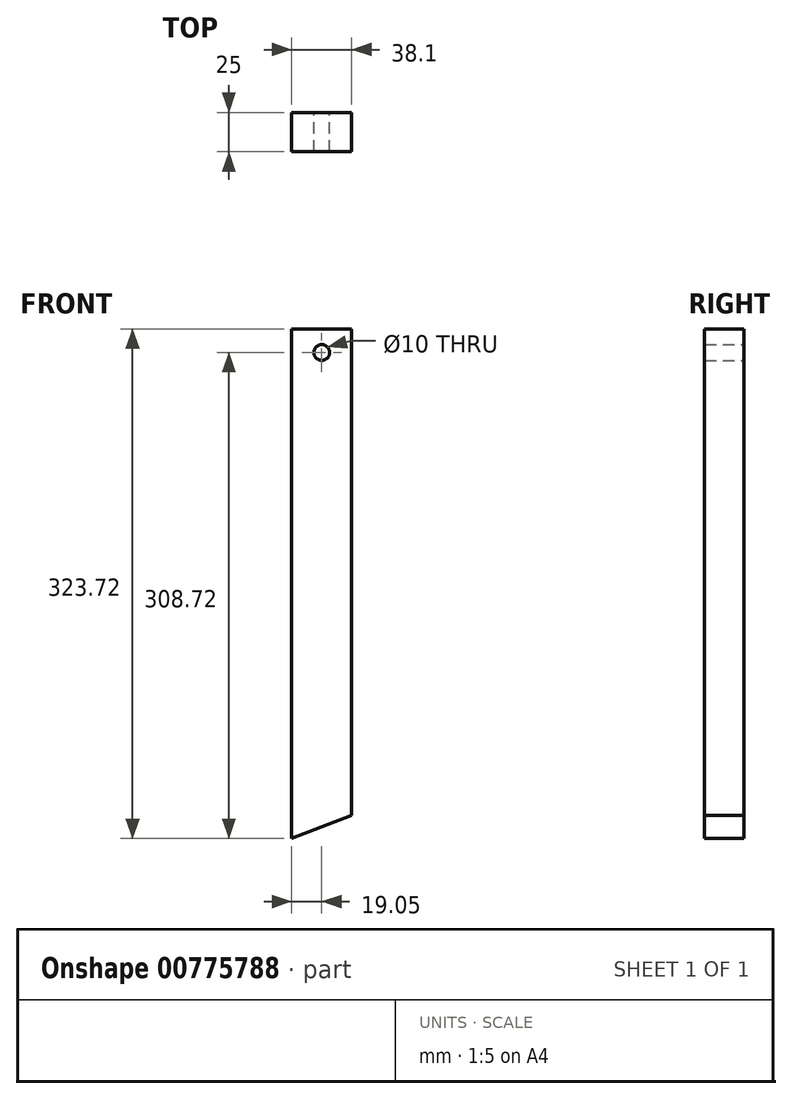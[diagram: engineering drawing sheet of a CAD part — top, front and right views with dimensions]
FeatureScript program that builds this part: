
annotation { "Feature Type Name" : "Feature", "Feature Type Description" : "" }
export const myFeature = defineFeature(function(context is Context, id is Id, definition is map)
    precondition{}
    {
        {
            var Q0;
            Q0=qCreatedBy(makeId("Front.planeOp"),FACE);
            var sketch = newSketch(context, id + "F0", { "sketchPlane" : qUnion([Q0])});
            skLineSegment(sketch, "E0", {"start": v(0, 0) * mm, "end": v(0, -323.72) * mm});
            skLineSegment(sketch, "E1", {"start": v(0, -323.72) * mm, "end": v(38.1, -309.11) * mm});
            skLineSegment(sketch, "E2", {"start": v(38.1, -309.11) * mm, "end": v(38.1, 0) * mm});
            skLineSegment(sketch, "E3", {"start": v(38.1, 0) * mm, "end": v(0, 0) * mm});
            skCircle(sketch, "E4", {"center": v(19.05, -15) * mm, "radius": 5 * mm});
            skSolve(sketch);
        }
        {
            var Q0;
            Q0 = qSketchRegion(id + "F0", true);
            extrude(context, id + "F1", {"entities" : qUnion([Q0]), "depth" : 25 * mm, "offsetDistance" : 25 * mm});
        }
    });
